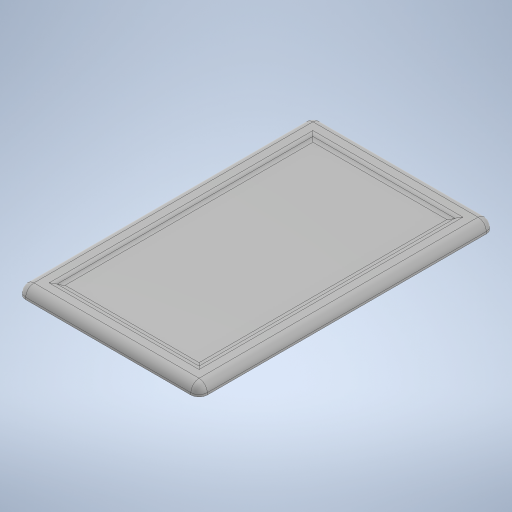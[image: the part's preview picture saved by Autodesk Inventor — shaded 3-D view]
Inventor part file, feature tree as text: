
AUTODESK INVENTOR PART (.ipt)
format: ipt  version: 2024 (Build 280153000, 153)  size: 283,136 bytes
history: native  units: in
note: dims shown in document units (in); Inventor stores cm internally (conversion verified against a paired STEP export)
features: extrude x2, fillet x2, sketch x2, projected_geometry x1, other x1
ambient origin geometry x8: Origin, YZ Plane, XZ Plane, XY Plane, X Axis, Y Axis, Z Axis, Center Point
bodies: Solid1 (feature_tree)
feature tree (8):
  extrude  "Extrusion1"  Depth=14.278in
  fillet  "Fillet1"  Radius=0.5in
  extrude  "Extrusion2"  Depth=0.1in TaperAngle=0.0deg
  fillet  "Fillet2"  Radius=0.4in
  sketch  "Sketch2"  dims[d0=8.778in d1=14.278in d2=0.5in d3=0.0in]
  sketch  "Sketch3"  dims[d4=0.4in d5=0.1in d6=0.0in d7=0.4in]
  projected_geometry  "Projected Loop1"
  other  "Finish1"
